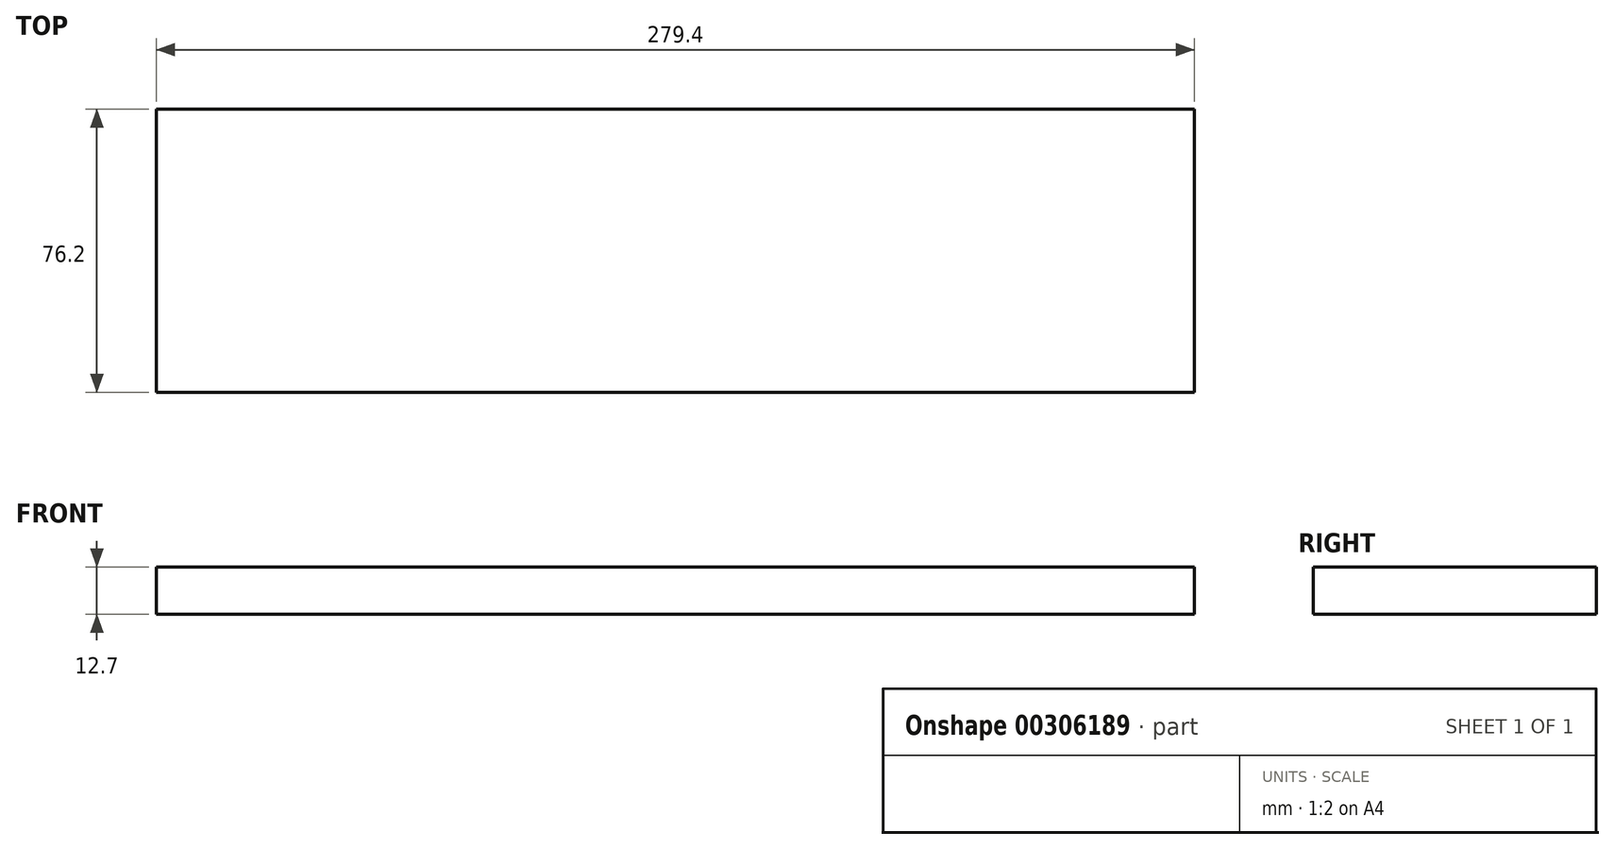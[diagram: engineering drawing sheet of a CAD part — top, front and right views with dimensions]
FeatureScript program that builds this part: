
annotation { "Feature Type Name" : "Feature", "Feature Type Description" : "" }
export const myFeature = defineFeature(function(context is Context, id is Id, definition is map)
    precondition{}
    {
        {
            var Q0;
            Q0=qCreatedBy(makeId("Top.planeOp"),FACE);
            var sketch = newSketch(context, id + "F0", { "sketchPlane" : qUnion([Q0])});
            skLineSegment(sketch, "E0.bottom", {"start": v(-139.7, 38.1) * mm, "end": v(139.7, 38.1) * mm});
            skLineSegment(sketch, "E0.top", {"start": v(-139.7, -38.1) * mm, "end": v(139.7, -38.1) * mm});
            skLineSegment(sketch, "E0.left", {"start": v(-139.7, 38.1) * mm, "end": v(-139.7, -38.1) * mm});
            skLineSegment(sketch, "E0.right", {"start": v(139.7, 38.1) * mm, "end": v(139.7, -38.1) * mm});
            skPoint(sketch, "E0.middle", {"position": v(0, 0) * mm});
            skSolve(sketch);
        }
        {
            var Q0;
            Q0=makeQuery(id+"F0.imprint","IMPRINT",FACE,{"disambiguationData":[TD([[makeQuery(id+"F0.imprint","IMPRINT",EDGE,{"derivedFrom":sQuery(id+"F0.wireOp",EDGE,"E0.bottom")}),-1.0]])]});
            extrude(context, id + "F1", {"entities" : qUnion([Q0]), "depth" : 12.7 * mm});
        }
    });
